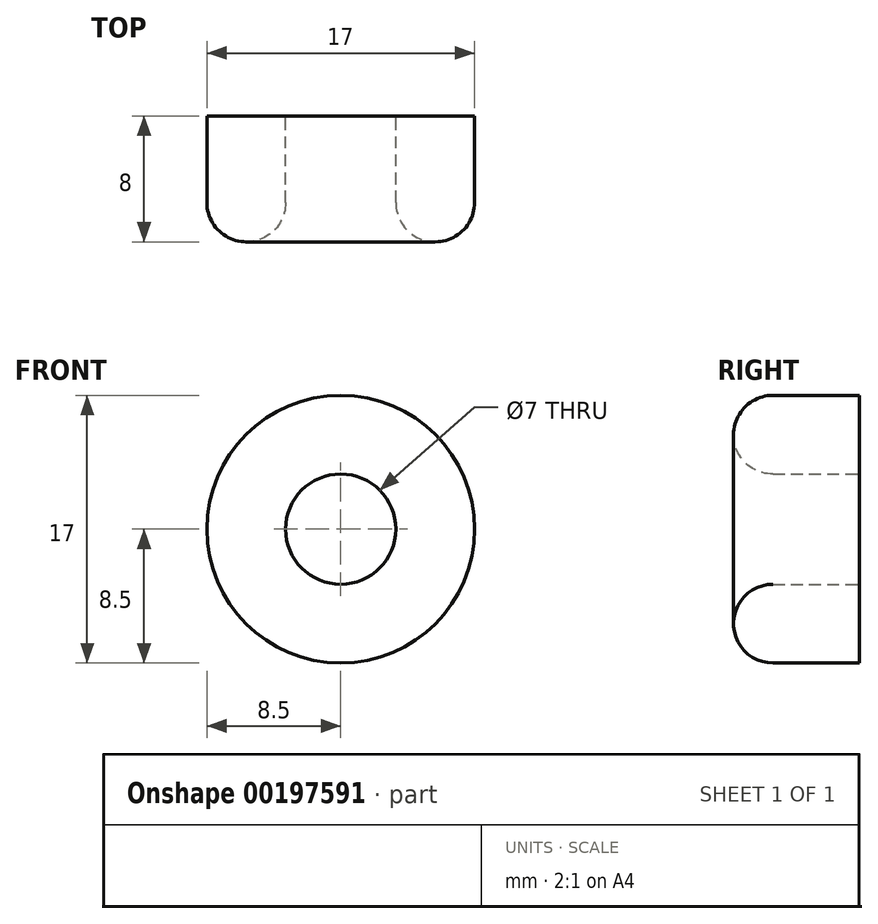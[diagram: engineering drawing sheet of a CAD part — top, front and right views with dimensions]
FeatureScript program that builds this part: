
annotation { "Feature Type Name" : "Feature", "Feature Type Description" : "" }
export const myFeature = defineFeature(function(context is Context, id is Id, definition is map)
    precondition{}
    {
        {
            var Q0;
            Q0=qCreatedBy(makeId("Front.planeOp"),FACE);
            var sketch = newSketch(context, id + "F0", { "sketchPlane" : qUnion([Q0])});
            skCircle(sketch, "E0", {"center": v(0, 0) * mm, "radius": 8.5 * mm});
            skCircle(sketch, "E1", {"center": v(0, 0) * mm, "radius": 3.5 * mm});
            skSolve(sketch);
        }
        {
            var Q0;
            Q0=makeQuery(id+"F0.imprint","IMPRINT",FACE,{"disambiguationData":[TD([[makeQuery(id+"F0.imprint","IMPRINT",EDGE,{"derivedFrom":sQuery(id+"F0.wireOp",EDGE,"E0")}),1.0]])]});
            extrude(context, id + "F1", {"entities" : qUnion([Q0]), "depth" : 8 * mm});
        }
        {
            var Q0;
            Q0=makeQuery(id+"F1.opExtrude","CAP_EDGE",EDGE,{"disambiguationData":[OSD([sQuery(id+"F0.wireOp",EDGE,"E0")])],"isStart":false});
            fillet(context, id + "F2", {"entities" : qUnion([Q0]), "radius" : 2.5 * mm, "tangentPropagation" : true, "allowEdgeOverflow" : false});
        }
        {
            var Q0;
            Q0=makeQuery(id+"F1.opExtrude","CAP_EDGE",EDGE,{"disambiguationData":[OSD([sQuery(id+"F0.wireOp",EDGE,"E1")])],"isStart":false});
            fillet(context, id + "F3", {"entities" : qUnion([Q0]), "radius" : 2.5 * mm, "tangentPropagation" : true, "allowEdgeOverflow" : false});
        }
    });
